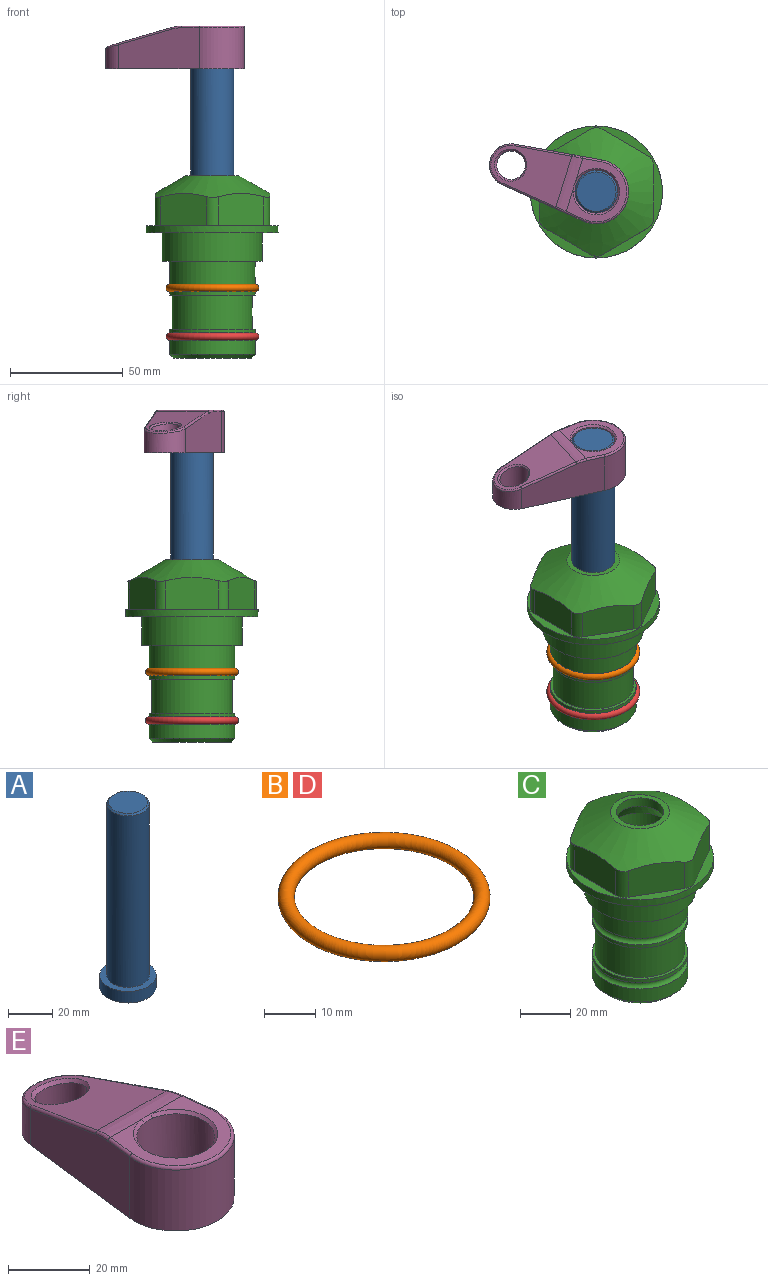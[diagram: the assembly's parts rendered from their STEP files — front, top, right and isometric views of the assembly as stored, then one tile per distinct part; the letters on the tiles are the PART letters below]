
ASSEMBLY  parts=5 mates=4
PART A: 6 faces, bbox 25.4x25.4x101.6 mm
  f0: plane 17.46x17.46mm, normal (0,0,1), area 239.5mm2, adj f5
  f1: plane 25.4x25.4mm, normal (0,0,-1), area 506.7mm2, adj f2
  f2: cylinder r=12.7mm len=25.4mm, axis (0,0,1), area 506.7mm2, adj f1,f3
  f3: plane 25.4x25.4mm, normal (0,0,1), area 221.7mm2, adj f2,f4
  f4: cylinder r=9.53mm len=94.46mm, axis (0,0,1), area 5653mm2, adj f3,f5
  f5: cone r=8.73mm half-angle=45deg, axis (0,0,-1), area 64.4mm2, adj f0,f4
PART B: 1 faces, bbox 44.7x44.7x3.2 mm
  f0: torus R=19.05mm, axis (0,0,1), area 1193.9mm2
PART C: 36 faces, bbox 58.7x58.7x81 mm
  f0: cylinder r=17.78mm len=35.56mm, axis (0,0,1), area 1670.8mm2, adj f23,f24,f31
  f1: cylinder r=19.05mm len=38.1mm, axis (0,0,1), area 1191.9mm2, adj f26,f27,f30
  f2: plane 58.66x58.66mm, normal (0,0,-1), area 1150.6mm2, adj f3,f28
  f3: cylinder r=29.33mm len=58.66mm, axis (0,0,-1), area 585.1mm2, adj f2,f4
  f4: plane 58.66x58.66mm, normal (0,0,1), area 475.9mm2, adj f3,f5,f6,f7,f8,f9,f10,f11
  f5: plane 20.32x14.34mm, normal (-0.5,0.87,0), area 324.4mm2, adj f4,f15,f16,f17
  f6: plane 20.32x14.34mm, normal (0.5,0.87,0), area 324.4mm2, adj f4,f14,f15,f17
  f7: plane 23.48x14.34mm, normal (1,0,0), area 324.4mm2, adj f4,f13,f14,f17
  f8: plane 20.32x14.34mm, normal (0.5,-0.87,0), area 324.4mm2, adj f4,f12,f13,f17
  f9: plane 20.32x14.34mm, normal (-0.5,-0.87,0), area 324.4mm2, adj f4,f11,f12,f17
  f10: plane 23.48x14.34mm, normal (-1,0,0), area 324.4mm2, adj f4,f11,f16,f17
  f11: cylinder r=5.08mm len=12.85mm, axis (0,0,-1), area 67.2mm2, adj f4,f9,f10,f17
  f12: cylinder r=5.08mm len=12.85mm, axis (0,0,-1), area 67.2mm2, adj f4,f8,f9,f17
  f13: cylinder r=5.08mm len=12.85mm, axis (0,0,-1), area 67.2mm2, adj f4,f7,f8,f17
  f14: cylinder r=5.08mm len=12.85mm, axis (0,0,-1), area 67.2mm2, adj f4,f6,f7,f17
  f15: cylinder r=5.08mm len=12.85mm, axis (0,0,-1), area 67.2mm2, adj f4,f5,f6,f17
  f16: cylinder r=5.08mm len=12.85mm, axis (0,0,-1), area 67.2mm2, adj f4,f5,f10,f17
  f17: cone r=11.73mm half-angle=60deg, axis (0,0,-1), area 2071.8mm2, adj f5,f6,f7,f8,f9,f10,f11,f12
  f18: plane 23.46x23.46mm, normal (0,0,1), area 147.4mm2, adj f17,f35
  f19: plane 34.93x34.93mm, normal (0,0,-1), area 958mm2, adj f29
  f20: cylinder r=19.05mm len=38.1mm, axis (0,0,1), area 760.1mm2, adj f21,f29
  f21: torus R=19.05mm, axis (0,0,1), area 565.3mm2, adj f20,f22
  f22: cylinder r=19.05mm len=38.1mm, axis (0,0,1), area 190mm2, adj f21,f23
  f23: plane 38.1x38.1mm, normal (0,0,1), area 146.9mm2, adj f0,f22
  f24: plane 38.1x38.1mm, normal (0,0,-1), area 146.9mm2, adj f0,f25
  f25: cylinder r=19.05mm len=38.1mm, axis (0,0,1), area 190mm2, adj f24,f26
  f26: torus R=19.05mm, axis (0,0,1), area 565.3mm2, adj f1,f25
  f27: plane 44.45x44.45mm, normal (0,0,-1), area 411.7mm2, adj f1,f28
  f28: cylinder r=22.23mm len=44.45mm, axis (0,0,1), area 1773.5mm2, adj f2,f27
  f29: cone r=19.05mm half-angle=45deg, axis (0,0,1), area 257.5mm2, adj f19,f20
  f30: cylinder r=3.17mm len=6.75mm, axis (-1,0,0), area 128mm2, adj f1,f33
  f31: cylinder r=3.17mm len=6.35mm, axis (-1,0,0), area 102.5mm2, adj f0,f33
  f32: plane 25.4x25.4mm, normal (0,0,1), area 506.7mm2, adj f33
  f33: cylinder r=12.7mm len=66.42mm, axis (0,0,-1), area 5236.2mm2, adj f30,f31,f32,f34
  f34: cone r=9.53mm half-angle=30deg, axis (0,0,-1), area 443.4mm2, adj f33,f35
  f35: cylinder r=9.53mm len=19.05mm, axis (0,0,-1), area 240.9mm2, adj f18,f34
PART D: same geometry as B
PART E: 31 faces, bbox 31.7x65.5x19.8 mm
  f0: plane 39.12x18.26mm, normal (0.99,0.12,0), area 612.2mm2, adj f1,f4,f7,f11,f13,f15
  f1: cylinder r=9.53mm len=18.91mm, axis (0,0,-1), area 296.1mm2, adj f0,f2,f7,f17
  f2: plane 39.12x18.26mm, normal (-0.99,0.12,0), area 612.2mm2, adj f1,f4,f7,f12,f14,f16
  f3: cylinder r=6.35mm len=12.7mm, axis (0,0,-1), area 362.4mm2, adj f7,f18
  f4: cylinder r=14.29mm len=28.58mm, axis (0,0,-1), area 882.2mm2, adj f0,f2,f7,f10
  f5: cylinder r=9.53mm len=19.05mm, axis (0,0,-1), area 1092.6mm2, adj f7,f19,f20
  f6: plane 26.99x23.69mm, normal (0,0,1), area 216.2mm2, adj f9,f10,f11,f12,f19
  f7: plane 63.5x28.58mm, normal (0,0,-1), area 661.8mm2, adj f0,f1,f2,f3,f4,f5,f22,f23
  f8: plane 33.52x23.6mm, normal (0,0.26,0.97), area 486mm2, adj f9,f15,f16,f17,f18
  f9: cylinder r=19.05mm len=24.72mm, axis (1,0,0), area 120.4mm2, adj f6,f8,f13,f14,f20
  f10: torus R=13.49mm, axis (0,0,1), area 59mm2, adj f4,f6,f11,f12
  f11: cylinder r=0.79mm len=8.67mm, axis (0.12,-0.99,0), area 10.8mm2, adj f0,f6,f10,f13
  f12: cylinder r=0.79mm len=8.67mm, axis (0.12,0.99,0), area 10.8mm2, adj f2,f6,f10,f14
  f13: bspline ~4.95x1.42mm, area 6.1mm2, adj f0,f9,f11,f15
  f14: bspline ~4.95x1.42mm, area 6.1mm2, adj f2,f9,f12,f16
  f15: cylinder r=0.79mm len=25.95mm, axis (0.12,-0.96,0.26), area 32.9mm2, adj f0,f8,f13,f17
  f16: cylinder r=0.79mm len=25.95mm, axis (0.12,0.96,-0.26), area 32.9mm2, adj f2,f8,f14,f17
  f17: bspline ~18.91x8.38mm, area 30mm2, adj f1,f8,f15,f16
  f18: bspline ~14.29x14.29mm, area 48.3mm2, adj f3,f8
  f19: cone r=9.53mm half-angle=45deg, axis (0,0,1), area 66.5mm2, adj f5,f6,f20
  f20: bspline ~3.22x0.96mm, area 3.5mm2, adj f5,f9,f19
  f21: plane 2.75x2.72mm, normal (0,0,-1), area 2.9mm2, adj f23,f25,f28
  f22: plane 23.05x15.88mm, normal (-0.99,-0.12,0), area 323.6mm2, adj f7,f25,f26,f27,f28,f29
  f23: plane 23.05x15.88mm, normal (0.99,-0.12,0), area 323.6mm2, adj f7,f21,f25,f27,f28,f30
  f24: cylinder r=9.53mm len=10.69mm, axis (0,0,-1), area 114.7mm2, adj f7,f27,f29,f30
  f25: cylinder r=12.7mm len=20.59mm, axis (0,0,-1), area 381.1mm2, adj f7,f21,f22,f23,f26,f28
  f26: plane 2.75x2.72mm, normal (0,0,-1), area 2.9mm2, adj f22,f25,f28
  f27: plane 19.72x18.37mm, normal (0,-0.26,-0.97), area 291.8mm2, adj f22,f23,f24,f28,f29,f30
  f28: cylinder r=15.88mm len=19.92mm, axis (1,0,0), area 54.8mm2, adj f21,f22,f23,f25,f26,f27
  f29: cylinder r=1.59mm len=11mm, axis (0,0,-1), area 34.7mm2, adj f7,f22,f24,f27
  f30: cylinder r=1.59mm len=11mm, axis (0,0,-1), area 34.7mm2, adj f7,f23,f24,f27
PLACE A rot(axis=(0,0,1),72.8deg) t=(0,0,27.55)mm
PLACE B at identity
PLACE C at identity fixed
PLACE D t=(0,0,-21.59)mm
PLACE E rot(axis=(0,0,1),72.8deg) t=(0,0,28.35)mm
MATE fastened D.f0 <-> C.f0  axis (0,0,1) through (0,0,-46.1)mm
MATE fastened A.f2 <-> E.f4  axis (0,0,1) through (0,0,91.05)mm
MATE cylindrical A.f2 <-> C.f0  axis (0,0,-1) through (0,0,-10.55)mm
MATE fastened B.f0 <-> C.f0  axis (0,0,1) through (0,0,-24.51)mm
